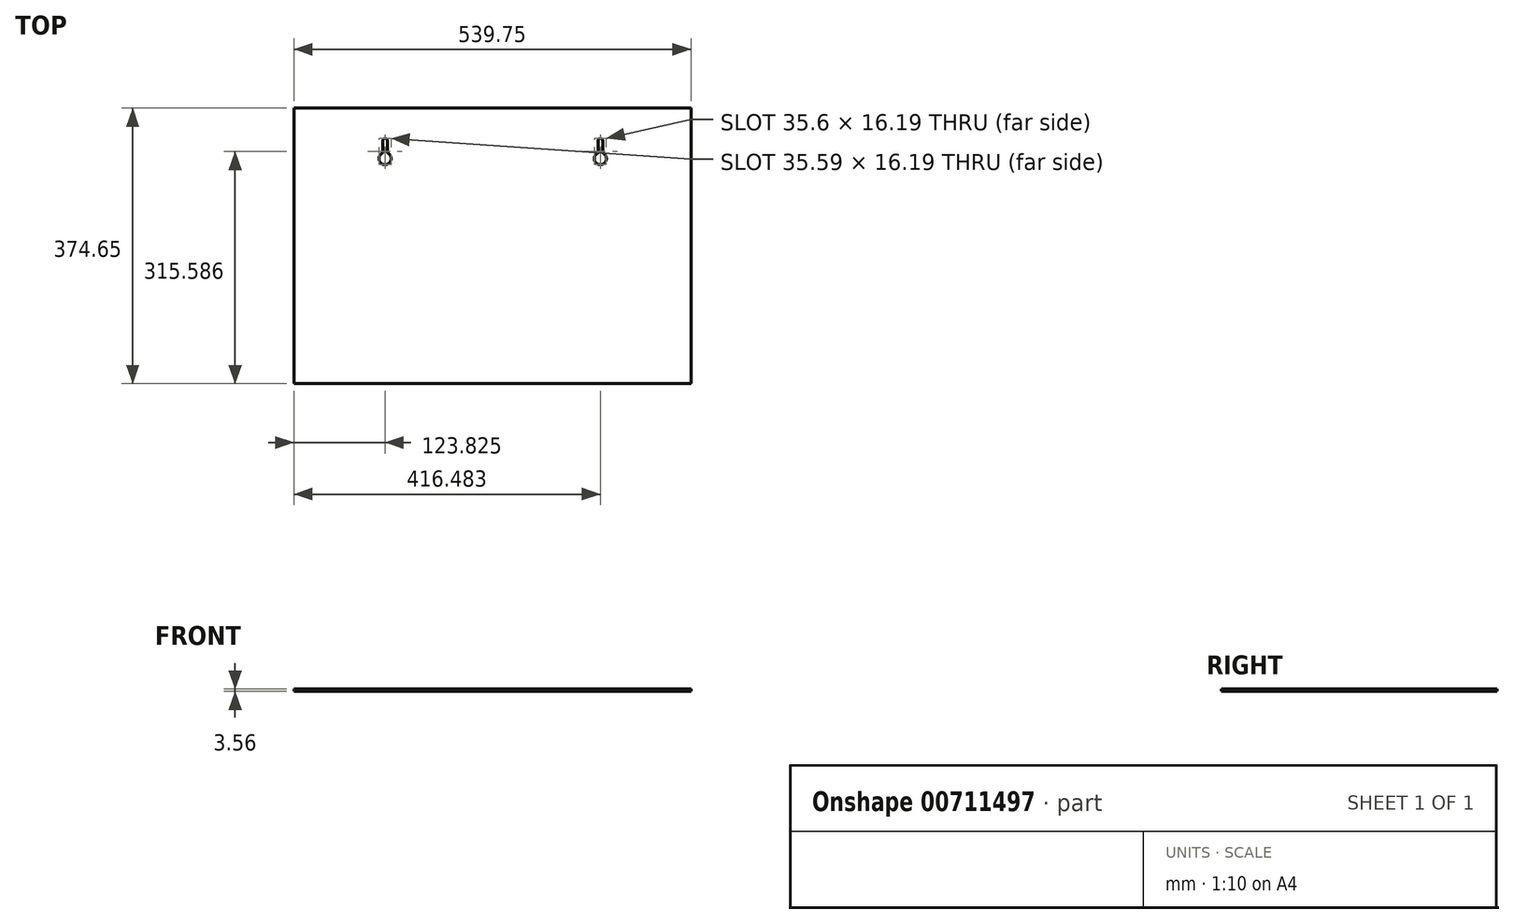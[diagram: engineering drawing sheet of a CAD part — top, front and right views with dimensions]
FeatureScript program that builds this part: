
annotation { "Feature Type Name" : "Feature", "Feature Type Description" : "" }
export const myFeature = defineFeature(function(context is Context, id is Id, definition is map)
    precondition{}
    {
        {
            var Q0;
            Q0=qCreatedBy(makeId("Top.planeOp"),FACE);
            var sketch = newSketch(context, id + "F0", { "sketchPlane" : qUnion([Q0])});
            skLineSegment(sketch, "E0.bottom", {"start": v(0, 0) * mm, "end": v(539.75, 0) * mm});
            skLineSegment(sketch, "E0.top", {"start": v(0, 374.65) * mm, "end": v(539.75, 374.65) * mm});
            skLineSegment(sketch, "E0.left", {"start": v(0, 0) * mm, "end": v(0, 374.65) * mm});
            skLineSegment(sketch, "E0.right", {"start": v(539.75, 0) * mm, "end": v(539.75, 374.65) * mm});
            skLineSegment(sketch, "E1", {"start": v(123.82, 374.65) * mm, "end": v(123.82, 330.2) * mm});
            skLineSegment(sketch, "E2", {"start": v(416.48, 374.65) * mm, "end": v(416.48, 330.2) * mm});
            skArc(sketch, "E3", {"start": v(127, 330.2) * mm, "mid": v(123.75, 333.38) * mm, "end": v(120.65, 330.05) * mm});
            skArc(sketch, "E4", {"start": v(419.66, 330.15) * mm, "mid": v(416.44, 333.38) * mm, "end": v(413.31, 330.07) * mm});
            skArc(sketch, "E5", {"start": v(120.65, 313.66) * mm, "mid": v(123.82, 297.79) * mm, "end": v(127, 313.66) * mm});
            skArc(sketch, "E6", {"start": v(413.31, 313.66) * mm, "mid": v(416.48, 297.79) * mm, "end": v(419.66, 313.66) * mm});
            skLineSegment(sketch, "E7", {"start": v(127, 330.2) * mm, "end": v(127, 313.66) * mm});
            skLineSegment(sketch, "E8", {"start": v(120.65, 330.36) * mm, "end": v(120.65, 313.66) * mm});
            skLineSegment(sketch, "E9", {"start": v(413.31, 330.35) * mm, "end": v(413.31, 313.66) * mm});
            skLineSegment(sketch, "E10", {"start": v(419.66, 330.27) * mm, "end": v(419.66, 313.66) * mm});
            skSolve(sketch);
        }
        {
            var Q0;
            Q0=makeQuery(id+"F0.imprint","IMPRINT",FACE,{"disambiguationData":[TD([[makeQuery(id+"F0.imprint","IMPRINT",EDGE,{"derivedFrom":sQuery(id+"F0.wireOp",EDGE,"E0.bottom")}),1.0]])]});
            extrude(context, id + "F1", {"entities" : qUnion([Q0]), "depth" : 3.56 * mm, "offsetDistance" : 25.4 * mm});
        }
    });
